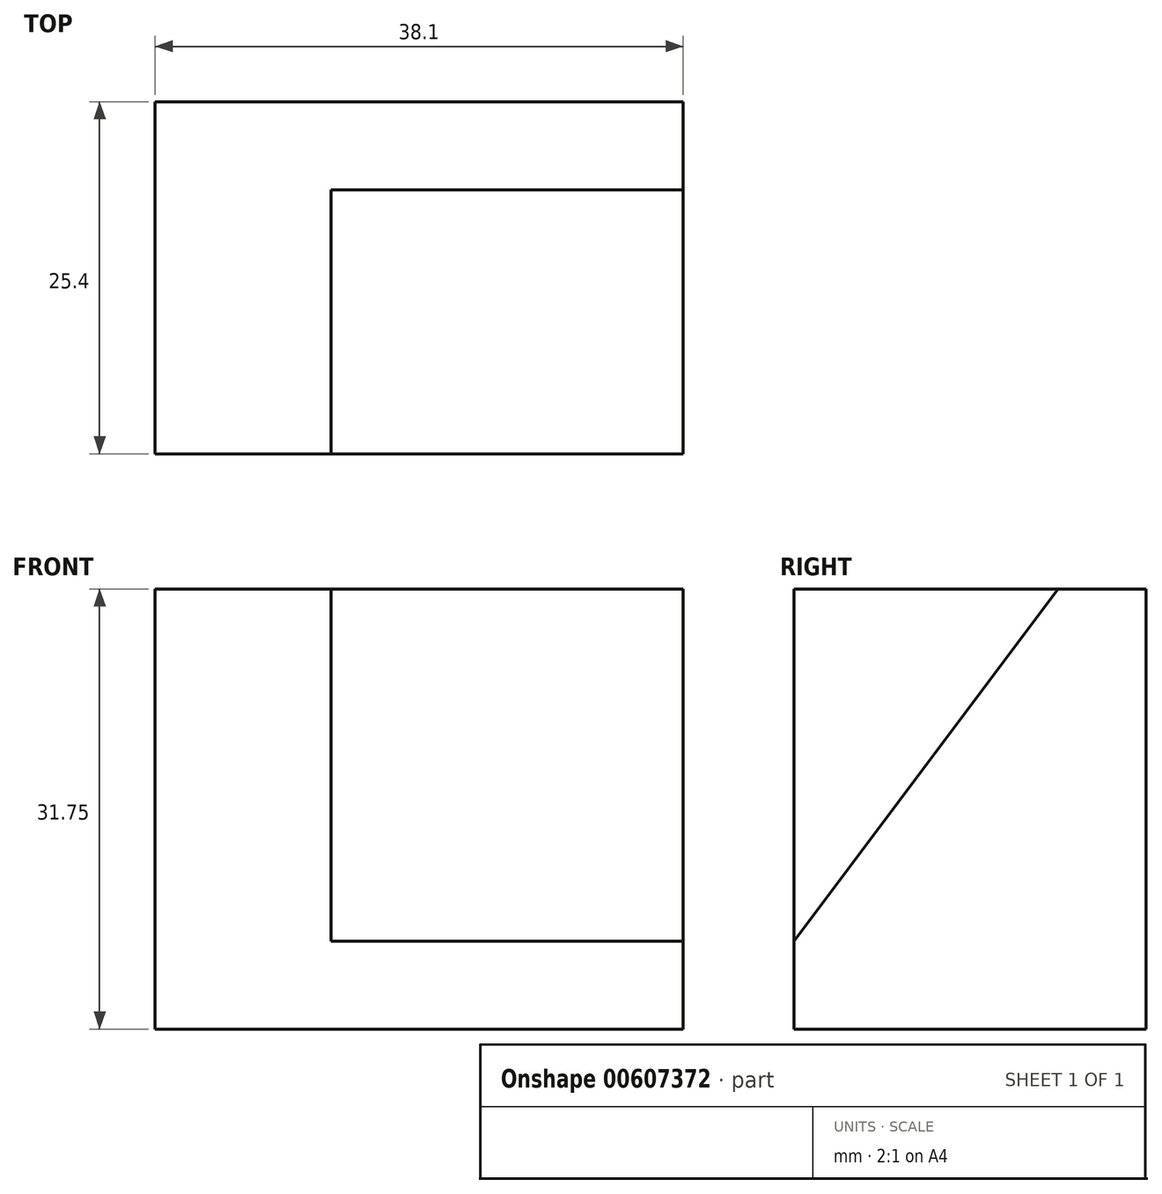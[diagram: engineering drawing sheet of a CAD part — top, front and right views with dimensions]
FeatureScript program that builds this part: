
annotation { "Feature Type Name" : "Feature", "Feature Type Description" : "" }
export const myFeature = defineFeature(function(context is Context, id is Id, definition is map)
    precondition{}
    {
        {
            var Q0;
            Q0=qCreatedBy(makeId("Front.planeOp"),FACE);
            var sketch = newSketch(context, id + "F0", { "sketchPlane" : qUnion([Q0])});
            skLineSegment(sketch, "E0.bottom", {"start": v(0, 0) * mm, "end": v(38.1, 0) * mm});
            skLineSegment(sketch, "E0.top", {"start": v(0, 31.75) * mm, "end": v(38.1, 31.75) * mm});
            skLineSegment(sketch, "E0.left", {"start": v(0, 0) * mm, "end": v(0, 31.75) * mm});
            skLineSegment(sketch, "E0.right", {"start": v(38.1, 0) * mm, "end": v(38.1, 31.75) * mm});
            skSolve(sketch);
        }
        {
            var Q0;
            Q0=makeQuery(id+"F0.imprint","IMPRINT",FACE,{"disambiguationData":[TD([[makeQuery(id+"F0.imprint","IMPRINT",EDGE,{"derivedFrom":sQuery(id+"F0.wireOp",EDGE,"E0.bottom")}),1.0]])]});
            extrude(context, id + "F1", {"entities" : qUnion([Q0]), "depth" : 25.4 * mm, "offsetDistance" : 25.4 * mm});
        }
        {
            var Q0;
            Q0=makeQuery(id+"F1.opExtrude","SWEPT_FACE",FACE,{"disambiguationData":[OSD([sQuery(id+"F0.wireOp",EDGE,"E0.right")])]});
            var sketch = newSketch(context, id + "F2", { "sketchPlane" : qUnion([Q0])});
            skLineSegment(sketch, "E1", {"start": v(0, 31.75) * mm, "end": v(-6.35, 31.75) * mm});
            skLineSegment(sketch, "E2", {"start": v(-25.4, 0) * mm, "end": v(-25.4, 6.35) * mm});
            skLineSegment(sketch, "E3", {"start": v(-25.4, 6.35) * mm, "end": v(-6.35, 31.75) * mm});
            skSolve(sketch);
        }
        {
            var Q0;
            Q0 = qSketchRegion(id + "F2", true);
            var Q1;
            {var subQ0=sQuery(id+"F2.wireOp",EDGE,"E3");Q1=makeQuery(id+"F2.imprint","IMPRINT",FACE,{"disambiguationData":[TD([[makeQuery(id+"F2.imprint","IMPRINT",EDGE,{"derivedFrom":subQ0}),1.0]])]});}
            extrude(context, id + "F3", {"entities" : qUnion([Q0, Q1]), "operationType" : NewBodyOperationType.REMOVE, "oppositeDirection" : true, "depth" : 25.4 * mm, "offsetDistance" : 25.4 * mm});
        }
    });
